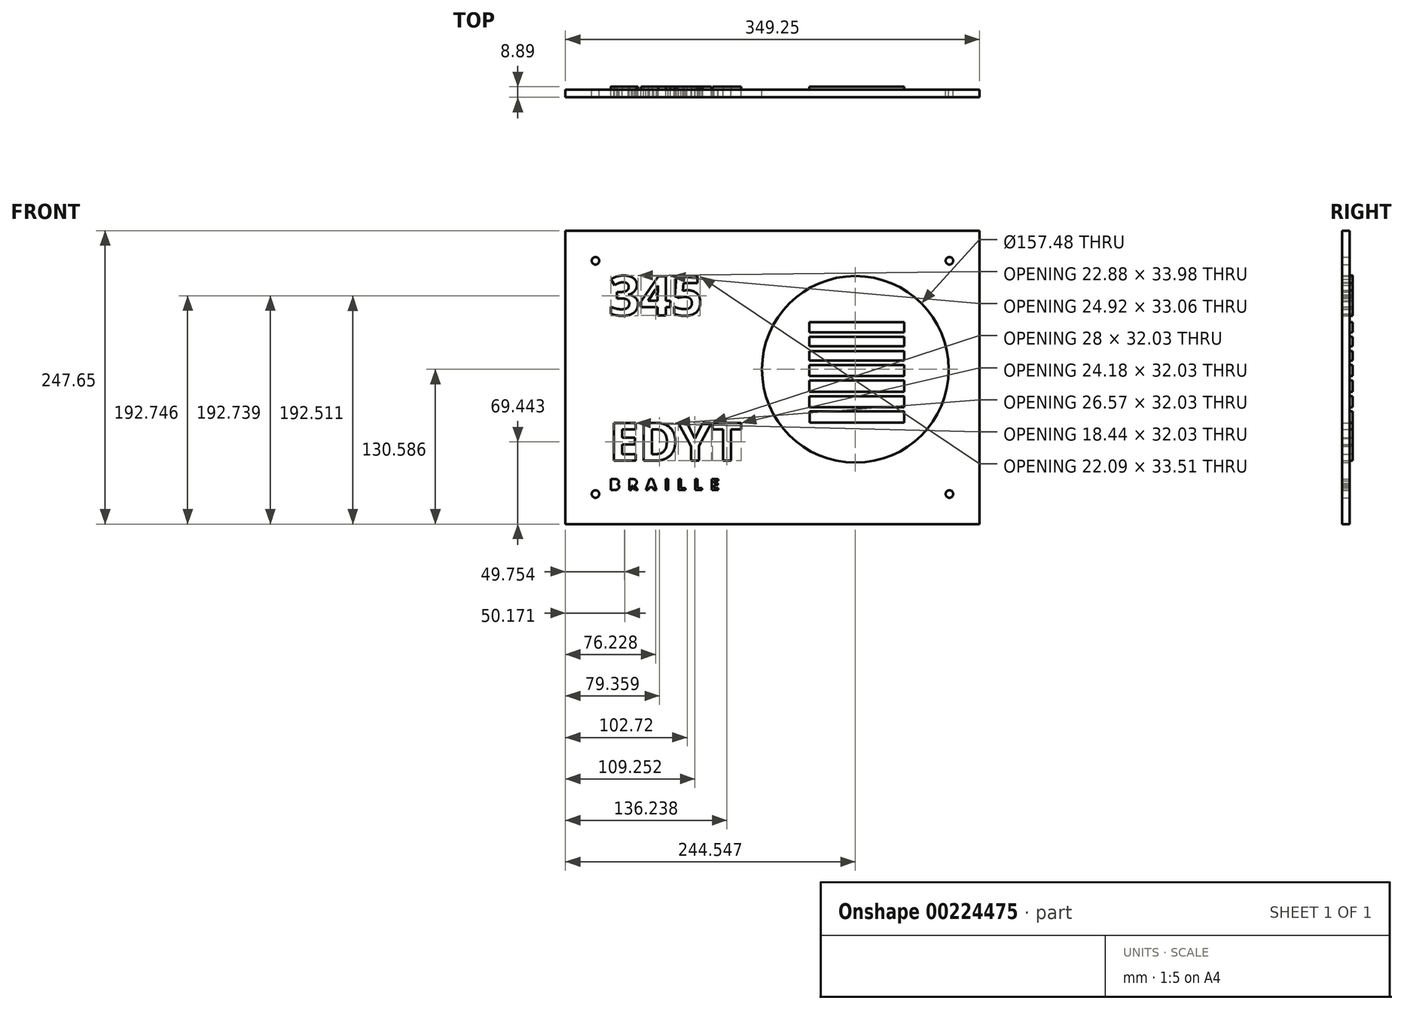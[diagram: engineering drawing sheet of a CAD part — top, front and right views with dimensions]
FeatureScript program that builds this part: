
annotation { "Feature Type Name" : "Feature", "Feature Type Description" : "" }
export const myFeature = defineFeature(function(context is Context, id is Id, definition is map)
    precondition{}
    {
        {
            var Q0;
            Q0=qCreatedBy(makeId("Front.planeOp"),FACE);
            var sketch = newSketch(context, id + "F0", { "sketchPlane" : qUnion([Q0])});
            skLineSegment(sketch, "E0.bottom", {"start": v(-62.9, 61.37) * mm, "end": v(286.35, 61.37) * mm});
            skLineSegment(sketch, "E0.top", {"start": v(-62.9, -186.28) * mm, "end": v(286.35, -186.28) * mm});
            skLineSegment(sketch, "E0.left", {"start": v(-62.9, 61.37) * mm, "end": v(-62.9, -186.28) * mm});
            skLineSegment(sketch, "E0.right", {"start": v(286.35, 61.37) * mm, "end": v(286.35, -186.28) * mm});
            skLineSegment(sketch, "E1", {"start": v(-37.5, 61.37) * mm, "end": v(-37.5, -186.28) * mm, "construction": true});
            skLineSegment(sketch, "E2", {"start": v(260.95, 61.37) * mm, "end": v(260.95, -186.28) * mm, "construction": true});
            skLineSegment(sketch, "E3", {"start": v(-62.9, 35.97) * mm, "end": v(286.35, 35.97) * mm, "construction": true});
            skLineSegment(sketch, "E4", {"start": v(-62.9, -160.88) * mm, "end": v(286.35, -160.88) * mm, "construction": true});
            skCircle(sketch, "E5", {"center": v(260.95, 35.97) * mm, "radius": 3.17 * mm});
            skCircle(sketch, "E6", {"center": v(260.95, -160.88) * mm, "radius": 3.18 * mm});
            skCircle(sketch, "E7", {"center": v(-37.5, -160.88) * mm, "radius": 3.18 * mm});
            skCircle(sketch, "E8", {"center": v(-37.5, 35.97) * mm, "radius": 3.18 * mm});
            skLineSegment(sketch, "E9", {"start": v(-62.9, -148.18) * mm, "end": v(286.35, -148.18) * mm, "construction": true});
            skLineSegment(sketch, "E10", {"start": v(-62.9, -138.66) * mm, "end": v(286.35, -138.66) * mm, "construction": true});
            skText(sketch, "E11", { "text": "B  R  A  I  L  L  E", "fontName": "OpenSans-Bold.ttf"});
            skLineSegment(sketch, "E12", {"start": v(-62.9, 23.27) * mm, "end": v(286.35, 23.27) * mm, "construction": true});
            skLineSegment(sketch, "E13", {"start": v(-62.9, -10.07) * mm, "end": v(286.35, -10.07) * mm, "construction": true});
            skText(sketch, "E14", { "text": "345", "fontName": "OpenSans-Bold.ttf"});
            skLineSegment(sketch, "E15", {"start": v(-62.9, -100.56) * mm, "end": v(286.35, -100.56) * mm, "construction": true});
            skText(sketch, "E16", { "text": "EDYT", "fontName": "OpenSans-Bold.ttf"});
            skCircle(sketch, "E17", {"center": v(181.65, -55.7) * mm, "radius": 78.74 * mm});
            skCircle(sketch, "E18", {"center": v(182.02, -55.7) * mm, "radius": 72.74 * mm});
            skCircle(sketch, "E19", {"center": v(181.27, -56.07) * mm, "radius": 66.88 * mm});
            skCircle(sketch, "E20", {"center": v(181.27, -55.7) * mm, "radius": 69 * mm});
            skLineSegment(sketch, "E21.bottom", {"start": v(143.25, -91.1) * mm, "end": v(222.65, -91.1) * mm});
            skLineSegment(sketch, "E21.top", {"start": v(143.25, -100.56) * mm, "end": v(222.65, -100.56) * mm});
            skLineSegment(sketch, "E21.left", {"start": v(143.25, -91.1) * mm, "end": v(143.25, -100.56) * mm});
            skLineSegment(sketch, "E21.right", {"start": v(222.65, -91.1) * mm, "end": v(222.65, -100.56) * mm});
            skLineSegment(sketch, "E22.bottom", {"start": v(142.88, -87.75) * mm, "end": v(222.65, -87.75) * mm});
            skLineSegment(sketch, "E22.top", {"start": v(142.88, -78.43) * mm, "end": v(222.65, -78.43) * mm});
            skLineSegment(sketch, "E22.left", {"start": v(142.88, -87.75) * mm, "end": v(142.88, -78.43) * mm});
            skLineSegment(sketch, "E22.right", {"start": v(222.65, -87.75) * mm, "end": v(222.65, -78.43) * mm});
            skLineSegment(sketch, "E23.bottom", {"start": v(142.88, -74.7) * mm, "end": v(222.65, -74.7) * mm});
            skLineSegment(sketch, "E23.top", {"start": v(142.88, -65.01) * mm, "end": v(222.65, -65.01) * mm});
            skLineSegment(sketch, "E23.left", {"start": v(142.88, -74.7) * mm, "end": v(142.88, -65.01) * mm});
            skLineSegment(sketch, "E23.right", {"start": v(222.65, -74.7) * mm, "end": v(222.65, -65.01) * mm});
            skLineSegment(sketch, "E24.bottom", {"start": v(142.88, -61.29) * mm, "end": v(222.65, -61.29) * mm});
            skLineSegment(sketch, "E24.top", {"start": v(142.88, -51.97) * mm, "end": v(222.65, -51.97) * mm});
            skLineSegment(sketch, "E24.left", {"start": v(142.88, -61.29) * mm, "end": v(142.88, -51.97) * mm});
            skLineSegment(sketch, "E24.right", {"start": v(222.65, -61.29) * mm, "end": v(222.65, -51.97) * mm});
            skLineSegment(sketch, "E25.bottom", {"start": v(142.88, -48.24) * mm, "end": v(222.65, -48.24) * mm});
            skLineSegment(sketch, "E25.top", {"start": v(142.88, -40.41) * mm, "end": v(222.65, -40.41) * mm});
            skLineSegment(sketch, "E25.left", {"start": v(142.88, -48.24) * mm, "end": v(142.88, -40.41) * mm});
            skLineSegment(sketch, "E25.right", {"start": v(222.65, -48.24) * mm, "end": v(222.65, -40.41) * mm});
            skLineSegment(sketch, "E26.bottom", {"start": v(142.88, -36.31) * mm, "end": v(222.65, -36.31) * mm});
            skLineSegment(sketch, "E26.top", {"start": v(142.88, -28.11) * mm, "end": v(222.65, -28.11) * mm});
            skLineSegment(sketch, "E26.left", {"start": v(142.88, -36.31) * mm, "end": v(142.88, -28.11) * mm});
            skLineSegment(sketch, "E26.right", {"start": v(222.65, -36.31) * mm, "end": v(222.65, -28.11) * mm});
            skLineSegment(sketch, "E27.bottom", {"start": v(142.88, -24.38) * mm, "end": v(222.65, -24.38) * mm});
            skLineSegment(sketch, "E27.top", {"start": v(142.88, -15.8) * mm, "end": v(222.65, -15.8) * mm});
            skLineSegment(sketch, "E27.left", {"start": v(142.88, -24.38) * mm, "end": v(142.88, -15.8) * mm});
            skLineSegment(sketch, "E27.right", {"start": v(222.65, -24.38) * mm, "end": v(222.65, -15.8) * mm});
            const initialGuessF0  = {"E11": [-0.0256, -0.15746, 1, 0, 0.00927], "E14": [-0.02635, -0.01007, 1, 0, 0.03334], "E16": [-0.02598, -0.13285, 1, 0, 0.0323]};
            skSetInitialGuess(sketch, initialGuessF0);
            skSolve(sketch);
        }
        {
            var Q0;
            Q0=makeQuery(id+"F0.imprint","IMPRINT",FACE,{"disambiguationData":[TD([[makeQuery(id+"F0.imprint","IMPRINT",EDGE,{"derivedFrom":sQuery(id+"F0.wireOp",EDGE,"E0.bottom")}),-1.0]])]});
            extrude(context, id + "F1", {"entities" : qUnion([Q0]), "depth" : 6.35 * mm});
        }
        {
            var Q0;
            Q0=makeQuery(id+"F0.imprint","IMPRINT",FACE,{"disambiguationData":[TD([[makeQuery(id+"F0.imprint","IMPRINT",EDGE,{"derivedFrom":sQuery(id+"F0.wireOp",EDGE,"E27.bottom")}),1.0]])]});
            var Q1;
            Q1=makeQuery(id+"F0.imprint","IMPRINT",FACE,{"disambiguationData":[TD([[makeQuery(id+"F0.imprint","IMPRINT",EDGE,{"derivedFrom":sQuery(id+"F0.wireOp",EDGE,"E26.bottom")}),1.0]])]});
            var Q2;
            Q2=makeQuery(id+"F0.imprint","IMPRINT",FACE,{"disambiguationData":[TD([[makeQuery(id+"F0.imprint","IMPRINT",EDGE,{"derivedFrom":sQuery(id+"F0.wireOp",EDGE,"E25.bottom")}),1.0]])]});
            var Q3;
            Q3=makeQuery(id+"F0.imprint","IMPRINT",FACE,{"disambiguationData":[TD([[makeQuery(id+"F0.imprint","IMPRINT",EDGE,{"derivedFrom":sQuery(id+"F0.wireOp",EDGE,"E24.bottom")}),1.0]])]});
            var Q4;
            Q4=makeQuery(id+"F0.imprint","IMPRINT",FACE,{"disambiguationData":[TD([[makeQuery(id+"F0.imprint","IMPRINT",EDGE,{"derivedFrom":sQuery(id+"F0.wireOp",EDGE,"E23.bottom")}),1.0]])]});
            var Q5;
            Q5=makeQuery(id+"F0.imprint","IMPRINT",FACE,{"disambiguationData":[TD([[makeQuery(id+"F0.imprint","IMPRINT",EDGE,{"derivedFrom":sQuery(id+"F0.wireOp",EDGE,"E22.bottom")}),1.0]])]});
            var Q6;
            Q6=makeQuery(id+"F0.imprint","IMPRINT",FACE,{"disambiguationData":[TD([[makeQuery(id+"F0.imprint","IMPRINT",EDGE,{"derivedFrom":sQuery(id+"F0.wireOp",EDGE,"E21.bottom")}),-1.0]])]});
            var Q7;
            Q7=makeQuery(id+"F0.imprint","IMPRINT",FACE,{"disambiguationData":[TD([[makeQuery(id+"F0.imprint","IMPRINT",EDGE,{"derivedFrom":sQuery(id+"F0.wireOp",EDGE,"E16.sketch_text.stroke-12")}),-1.0]])]});
            var Q8;
            Q8=makeQuery(id+"F0.imprint","IMPRINT",FACE,{"disambiguationData":[TD([[makeQuery(id+"F0.imprint","IMPRINT",EDGE,{"derivedFrom":sQuery(id+"F0.wireOp",EDGE,"E16.sketch_text.stroke-24")}),-1.0]])]});
            var Q9;
            Q9=makeQuery(id+"F0.imprint","IMPRINT",FACE,{"disambiguationData":[TD([[makeQuery(id+"F0.imprint","IMPRINT",EDGE,{"derivedFrom":sQuery(id+"F0.wireOp",EDGE,"E16.sketch_text.stroke-33")}),-1.0]])]});
            var Q10;
            Q10=makeQuery(id+"F0.imprint","IMPRINT",FACE,{"disambiguationData":[TD([[makeQuery(id+"F0.imprint","IMPRINT",EDGE,{"derivedFrom":sQuery(id+"F0.wireOp",EDGE,"E16.sketch_text.stroke-0")}),-1.0]])]});
            var Q11;
            Q11=makeQuery(id+"F0.imprint","IMPRINT",FACE,{"disambiguationData":[TD([[makeQuery(id+"F0.imprint","IMPRINT",EDGE,{"derivedFrom":sQuery(id+"F0.wireOp",EDGE,"E14.sketch_text.stroke-0")}),-1.0]])]});
            var Q12;
            Q12=makeQuery(id+"F0.imprint","IMPRINT",FACE,{"disambiguationData":[TD([[makeQuery(id+"F0.imprint","IMPRINT",EDGE,{"derivedFrom":sQuery(id+"F0.wireOp",EDGE,"E14.sketch_text.stroke-27")}),-1.0]])]});
            var Q13;
            Q13=makeQuery(id+"F0.imprint","IMPRINT",FACE,{"disambiguationData":[TD([[makeQuery(id+"F0.imprint","IMPRINT",EDGE,{"derivedFrom":sQuery(id+"F0.wireOp",EDGE,"E14.sketch_text.stroke-45")}),-1.0]])]});
            extrude(context, id + "F2", {"entities" : qUnion([Q0, Q1, Q2, Q3, Q4, Q5, Q6, Q7, Q8, Q9, Q10, Q11, Q12, Q13]), "oppositeDirection" : true, "depth" : 2.54 * mm});
        }
    });
